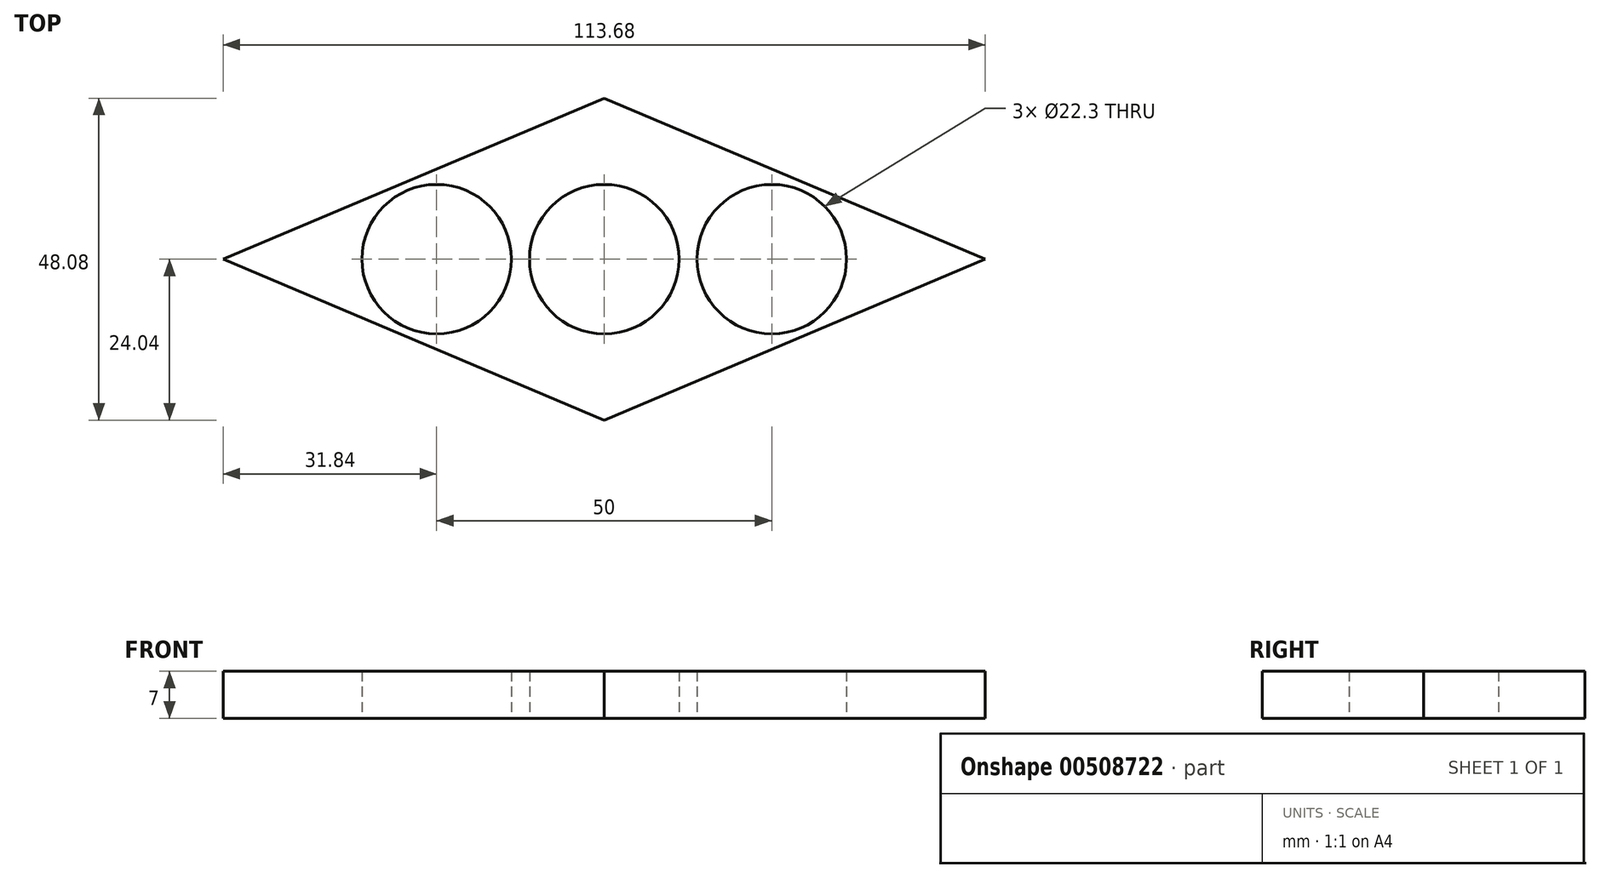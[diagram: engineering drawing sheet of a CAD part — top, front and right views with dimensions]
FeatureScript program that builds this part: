
annotation { "Feature Type Name" : "Feature", "Feature Type Description" : "" }
export const myFeature = defineFeature(function(context is Context, id is Id, definition is map)
    precondition{}
    {
        {
            var Q0;
            Q0=qCreatedBy(makeId("Top.planeOp"),FACE);
            var sketch = newSketch(context, id + "F0", { "sketchPlane" : qUnion([Q0])});
            skCircle(sketch, "E0", {"center": v(0, 0) * mm, "radius": 11.15 * mm});
            skLineSegment(sketch, "E1", {"start": v(0, 0) * mm, "end": v(11.15, 0) * mm, "construction": true});
            skLineSegment(sketch, "E2", {"start": v(0, 0) * mm, "end": v(25, 0) * mm});
            skLineSegment(sketch, "E3", {"start": v(0, 0) * mm, "end": v(-25, 0) * mm});
            skCircle(sketch, "E4", {"center": v(-25, 0) * mm, "radius": 11.15 * mm});
            skCircle(sketch, "E5", {"center": v(25, 0) * mm, "radius": 11.15 * mm});
            skLineSegment(sketch, "E6", {"start": v(-56.84, 0) * mm, "end": v(0, 24.04) * mm});
            skLineSegment(sketch, "E7.MirrorCS", {"start": v(56.84, 0) * mm, "end": v(0, 24.04) * mm});
            skLineSegment(sketch, "E8.MirrorCS", {"start": v(-56.84, 0) * mm, "end": v(0, -24.04) * mm});
            skLineSegment(sketch, "E9.MirrorCS", {"start": v(56.84, 0) * mm, "end": v(0, -24.04) * mm});
            skSolve(sketch);
        }
        {
            var Q0;
            Q0=makeQuery(id+"F0.imprint","IMPRINT",FACE,{"disambiguationData":[TD([[makeQuery(id+"F0.imprint","IMPRINT",EDGE,{"derivedFrom":sQuery(id+"F0.wireOp",EDGE,"E4")}),-1.0]])]});
            extrude(context, id + "F1", {"entities" : qUnion([Q0]), "depth" : 7 * mm});
        }
    });
